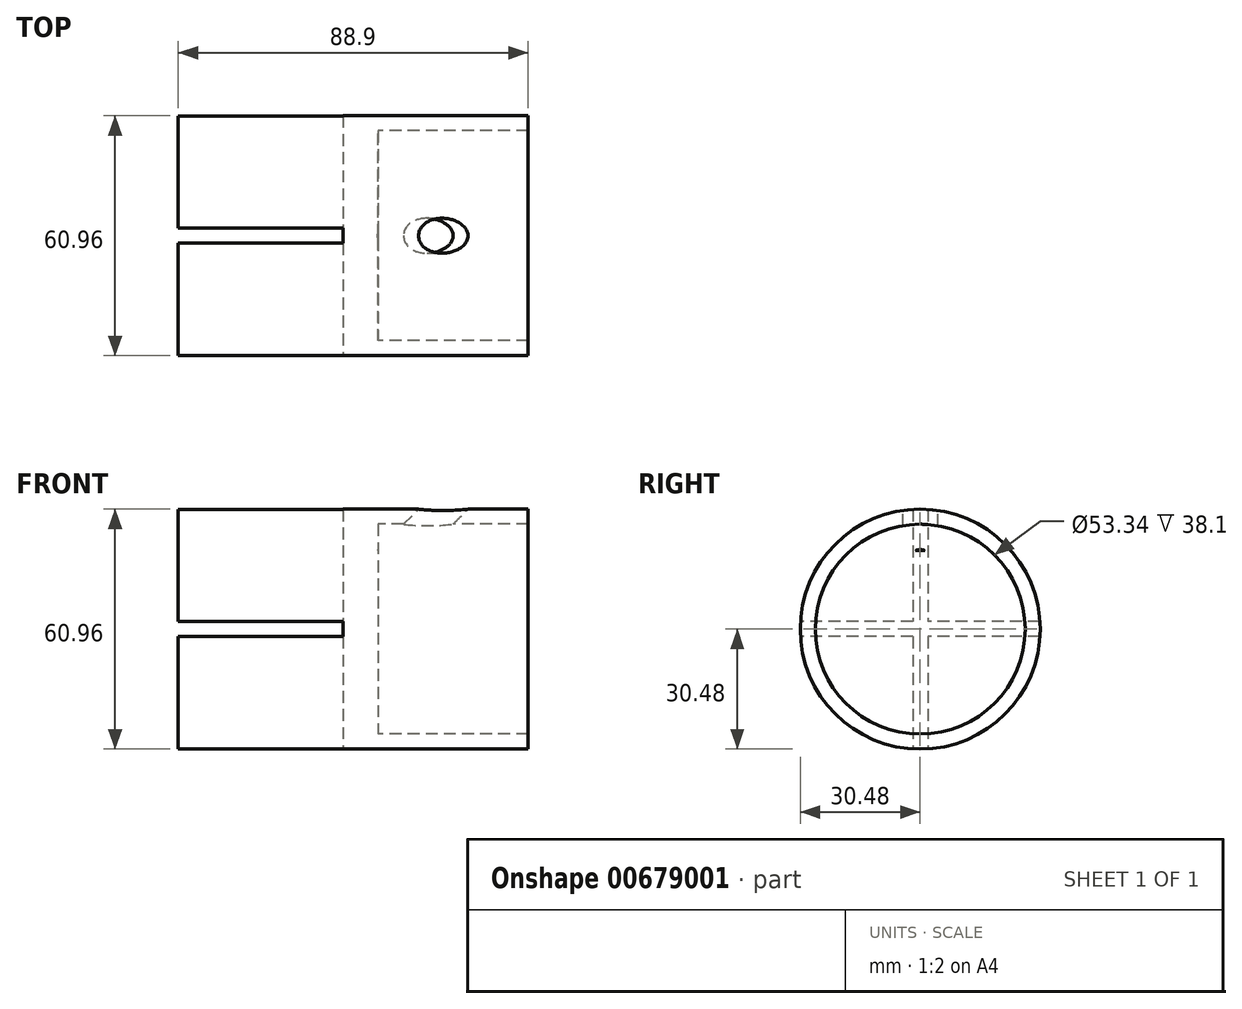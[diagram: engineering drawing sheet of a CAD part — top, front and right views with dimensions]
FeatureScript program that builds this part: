
annotation { "Feature Type Name" : "Feature", "Feature Type Description" : "" }
export const myFeature = defineFeature(function(context is Context, id is Id, definition is map)
    precondition{}
    {
        {
            var Q0;
            Q0=qCreatedBy(makeId("Front.planeOp"),FACE);
            var sketch = newSketch(context, id + "F0", { "sketchPlane" : qUnion([Q0])});
            skLineSegment(sketch, "E0", {"start": v(-51.3, 0) * mm, "end": v(63.75, 0) * mm, "construction": true});
            skLineSegment(sketch, "E1", {"start": v(-47.03, 0) * mm, "end": v(-47.03, 30.48) * mm});
            skLineSegment(sketch, "E2", {"start": v(-47.03, 30.48) * mm, "end": v(41.87, 30.48) * mm});
            skLineSegment(sketch, "E3", {"start": v(41.87, 30.48) * mm, "end": v(41.87, 26.67) * mm});
            skLineSegment(sketch, "E4", {"start": v(41.87, 26.67) * mm, "end": v(3.77, 26.67) * mm});
            skLineSegment(sketch, "E5", {"start": v(3.77, 26.67) * mm, "end": v(3.77, 0) * mm});
            skLineSegment(sketch, "E6", {"start": v(3.77, 0) * mm, "end": v(-47.03, 0) * mm});
            skSolve(sketch);
        }
        {
            var Q0;
            Q0=makeQuery(id+"F0.imprint","IMPRINT",FACE,{"disambiguationData":[TD([[makeQuery(id+"F0.imprint","IMPRINT",EDGE,{"derivedFrom":sQuery(id+"F0.wireOp",EDGE,"E1")}),-1.0]])]});
            var Q1;
            Q1=sQuery(id+"F0.wireOp",EDGE,"E0");
            revolve(context, id + "F1", {"entities" : qUnion([Q0]), "axis" : qUnion([Q1]), "revolveType" : RevolveType.FULL});
        }
        {
            var Q0;
            Q0=makeQuery(id+"F1.opRevolve","SWEPT_FACE",FACE,{"disambiguationData":[OSD([sQuery(id+"F0.wireOp",EDGE,"E1")])]});
            var sketch = newSketch(context, id + "F2", { "sketchPlane" : qUnion([Q0])});
            skLineSegment(sketch, "E7.bottom", {"start": v(-38.58, 1.9) * mm, "end": v(37.62, 1.9) * mm});
            skLineSegment(sketch, "E7.top", {"start": v(-38.58, -1.9) * mm, "end": v(37.62, -1.9) * mm});
            skLineSegment(sketch, "E7.left", {"start": v(-38.58, 1.9) * mm, "end": v(-38.58, -1.9) * mm});
            skLineSegment(sketch, "E7.right", {"start": v(37.62, 1.9) * mm, "end": v(37.62, -1.9) * mm});
            skLineSegment(sketch, "E8.bottom", {"start": v(-1.9, 34.5) * mm, "end": v(1.9, 34.5) * mm});
            skLineSegment(sketch, "E8.top", {"start": v(-1.9, -41.7) * mm, "end": v(1.9, -41.7) * mm});
            skLineSegment(sketch, "E8.left", {"start": v(-1.9, 34.5) * mm, "end": v(-1.9, -41.7) * mm});
            skLineSegment(sketch, "E8.right", {"start": v(1.9, 34.5) * mm, "end": v(1.9, -41.7) * mm});
            skSolve(sketch);
        }
        {
            var Q0;
            Q0 = qSketchRegion(id + "F2", true);
            extrude(context, id + "F3", {"entities" : qUnion([Q0]), "operationType" : NewBodyOperationType.REMOVE, "oppositeDirection" : true, "depth" : 41.9 * mm, "offsetDistance" : 25.4 * mm});
        }
        {
            var Q0;
            Q0=qCreatedBy(makeId("Front.planeOp"),FACE);
            var sketch = newSketch(context, id + "F4", { "sketchPlane" : qUnion([Q0])});
            skLineSegment(sketch, "E9", {"start": v(132.23, 142.39) * mm, "end": v(-10.16, 0) * mm, "construction": true});
            skSolve(sketch);
        }
        {
            var Q0;
            Q0=sQuery(id+"F4.wireOp",EDGE,"E9");
            cPlane(context, id + "F5", {"entities" : qUnion([Q0]), "cplaneType" : CPlaneType.MID_PLANE, "offset" : 25.4 * mm, "width" : 152.4 * mm, "height" : 152.4 * mm});
        }
        {
            var Q0;
            Q0=qCreatedBy(id+"F5.planeOp",FACE);
            var sketch = newSketch(context, id + "F6", { "sketchPlane" : qUnion([Q0])});
            skCircle(sketch, "E10", {"center": v(0, 7.18) * mm, "radius": 4.45 * mm});
            skSolve(sketch);
        }
        {
            var Q0;
            Q0=makeQuery(id+"F6.imprint","IMPRINT",FACE,{"disambiguationData":[TD([[makeQuery(id+"F6.imprint","IMPRINT",EDGE,{"derivedFrom":sQuery(id+"F6.wireOp",EDGE,"E10")}),1.0]])]});
            extrude(context, id + "F7", {"entities" : qUnion([Q0]), "operationType" : NewBodyOperationType.REMOVE, "depth" : 76.7 * mm, "offsetDistance" : 25.4 * mm});
        }
    });
